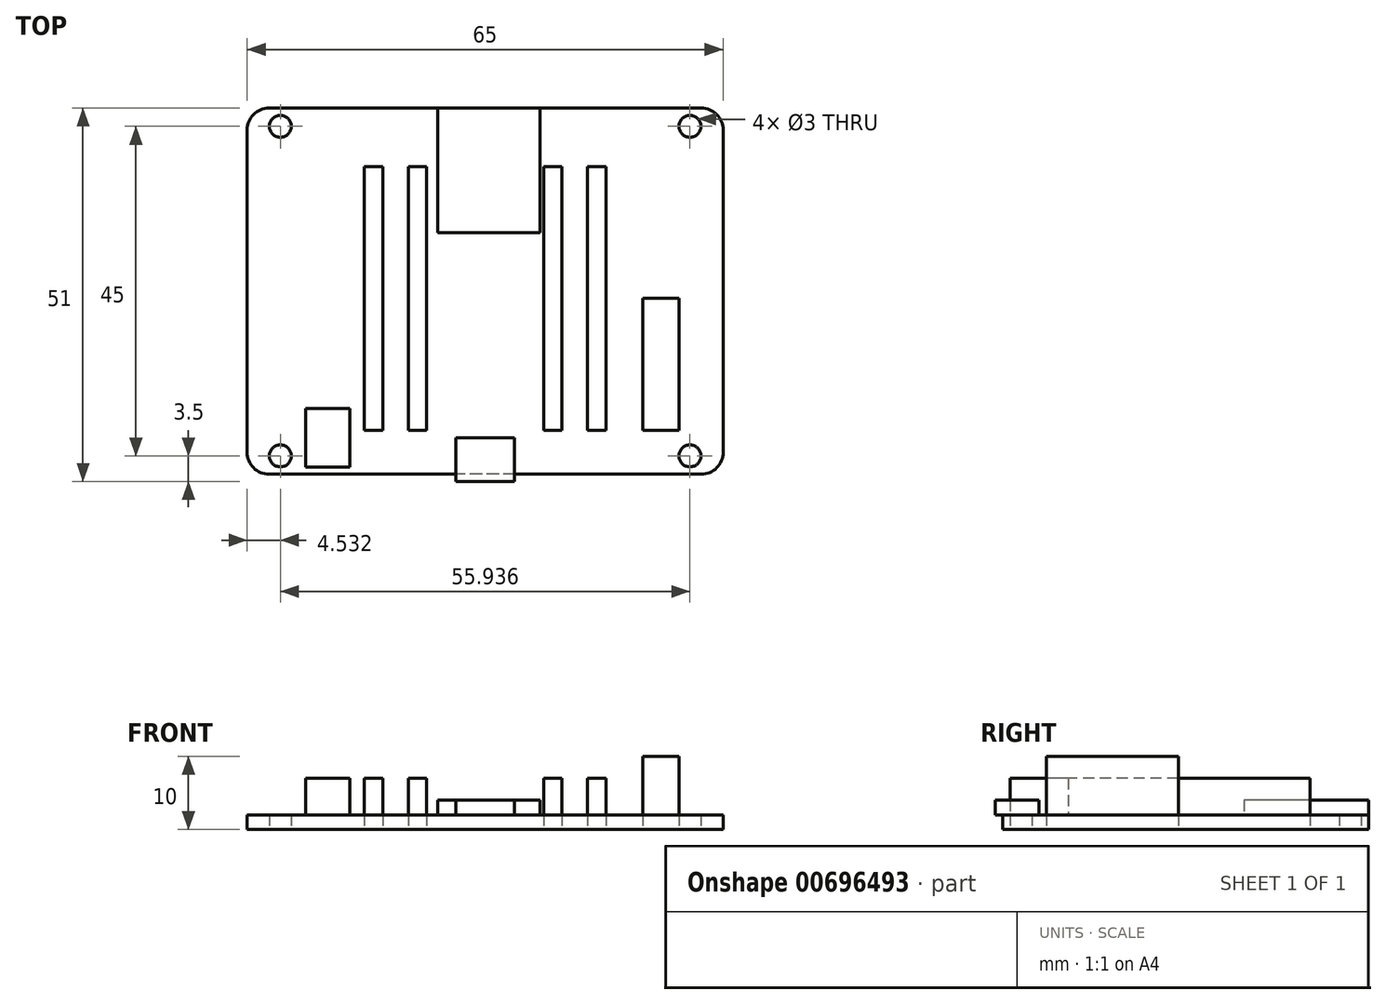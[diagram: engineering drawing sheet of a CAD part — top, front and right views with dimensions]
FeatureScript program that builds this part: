
annotation { "Feature Type Name" : "Feature", "Feature Type Description" : "" }
export const myFeature = defineFeature(function(context is Context, id is Id, definition is map)
    precondition{}
    {
        {
            var Q0;
            Q0=qCreatedBy(makeId("Top.planeOp"),FACE);
            var sketch = newSketch(context, id + "F0", { "sketchPlane" : qUnion([Q0])});
            skLineSegment(sketch, "E0.bottom", {"start": v(29.5, -25) * mm, "end": v(-29.5, -25) * mm});
            skLineSegment(sketch, "E0.top", {"start": v(29.5, 25) * mm, "end": v(-29.5, 25) * mm});
            skLineSegment(sketch, "E0.left", {"start": v(32.5, -22) * mm, "end": v(32.5, 22) * mm});
            skLineSegment(sketch, "E0.right", {"start": v(-32.5, -22) * mm, "end": v(-32.5, 22) * mm});
            skPoint(sketch, "E0.middle", {"position": v(0, 0) * mm});
            skPoint(sketch, "E1.visualSharp", {"position": v(-32.5, 25) * mm});
            skArc(sketch, "E1.filletArc", {"start": v(-29.5, 25) * mm, "mid": v(-31.62, 24.12) * mm, "end": v(-32.5, 22) * mm});
            skPoint(sketch, "E2.visualSharp", {"position": v(32.5, 25) * mm});
            skArc(sketch, "E2.filletArc", {"start": v(32.5, 22) * mm, "mid": v(31.62, 24.12) * mm, "end": v(29.5, 25) * mm});
            skPoint(sketch, "E3.visualSharp", {"position": v(32.5, -25) * mm});
            skArc(sketch, "E3.filletArc", {"start": v(29.5, -25) * mm, "mid": v(31.62, -24.12) * mm, "end": v(32.5, -22) * mm});
            skPoint(sketch, "E4.visualSharp", {"position": v(-32.5, -25) * mm});
            skArc(sketch, "E4.filletArc", {"start": v(-32.5, -22) * mm, "mid": v(-31.62, -24.12) * mm, "end": v(-29.5, -25) * mm});
            skCircle(sketch, "E5", {"center": v(-27.97, 22.5) * mm, "radius": 1.5 * mm});
            skLineSegment(sketch, "E6", {"start": v(-27.97, 24) * mm, "end": v(-27.97, 25) * mm, "construction": true});
            skLineSegment(sketch, "E7", {"start": v(-29.47, 22.45) * mm, "end": v(-32.47, 22.45) * mm, "construction": true});
            skLineSegment(sketch, "E8.MirrorCS", {"start": v(27.97, 24) * mm, "end": v(27.97, 25) * mm, "construction": true});
            skLineSegment(sketch, "E9.MirrorCS", {"start": v(29.47, 22.45) * mm, "end": v(32.47, 22.45) * mm, "construction": true});
            skCircle(sketch, "E10.MirrorC", {"center": v(27.97, 22.5) * mm, "radius": 1.5 * mm});
            skLineSegment(sketch, "E11.MirrorCS", {"start": v(-29.47, -22.45) * mm, "end": v(-32.47, -22.45) * mm, "construction": true});
            skLineSegment(sketch, "E12.MirrorCS", {"start": v(-27.97, -24) * mm, "end": v(-27.97, -25) * mm, "construction": true});
            skCircle(sketch, "E13.MirrorC", {"center": v(-27.97, -22.5) * mm, "radius": 1.5 * mm});
            skArc(sketch, "E14.MirrorCS", {"start": v(-29.5, -25) * mm, "mid": v(-31.62, -24.12) * mm, "end": v(-32.5, -22) * mm});
            skCircle(sketch, "E15.MirrorC", {"center": v(27.97, -22.5) * mm, "radius": 1.5 * mm});
            skLineSegment(sketch, "E16.bottom", {"start": v(21.5, -19) * mm, "end": v(26.5, -19) * mm});
            skLineSegment(sketch, "E16.top", {"start": v(21.5, -1) * mm, "end": v(26.5, -1) * mm});
            skLineSegment(sketch, "E16.left", {"start": v(21.5, -19) * mm, "end": v(21.5, -1) * mm});
            skLineSegment(sketch, "E16.right", {"start": v(26.5, -19) * mm, "end": v(26.5, -1) * mm});
            skLineSegment(sketch, "E17", {"start": v(24, -19) * mm, "end": v(24, -25) * mm, "construction": true});
            skLineSegment(sketch, "E18", {"start": v(26.5, -13.01) * mm, "end": v(32.5, -13.01) * mm, "construction": true});
            skLineSegment(sketch, "E19.bottom", {"start": v(-6.5, 26) * mm, "end": v(7.5, 26) * mm});
            skLineSegment(sketch, "E19.top", {"start": v(-6.5, 8) * mm, "end": v(7.5, 8) * mm});
            skLineSegment(sketch, "E19.left", {"start": v(-6.5, 26) * mm, "end": v(-6.5, 8) * mm});
            skLineSegment(sketch, "E19.right", {"start": v(7.5, 26) * mm, "end": v(7.5, 8) * mm});
            skLineSegment(sketch, "E20", {"start": v(-6.62, 26) * mm, "end": v(-6.62, 25) * mm, "construction": true});
            skLineSegment(sketch, "E21", {"start": v(7.5, 14.4) * mm, "end": v(32.5, 14.4) * mm, "construction": true});
            skLineSegment(sketch, "E22.bottom", {"start": v(14, 17) * mm, "end": v(16.5, 17) * mm});
            skLineSegment(sketch, "E22.top", {"start": v(14, -19) * mm, "end": v(16.5, -19) * mm});
            skLineSegment(sketch, "E22.left", {"start": v(14, 17) * mm, "end": v(14, -19) * mm});
            skLineSegment(sketch, "E22.right", {"start": v(16.5, 17) * mm, "end": v(16.5, -19) * mm});
            skLineSegment(sketch, "E23", {"start": v(15.25, -19) * mm, "end": v(15.25, -25) * mm, "construction": true});
            skLineSegment(sketch, "E24", {"start": v(16.5, 5.64) * mm, "end": v(32.5, 5.64) * mm, "construction": true});
            skLineSegment(sketch, "E25.1.0.0", {"start": v(8, 17) * mm, "end": v(8, -19) * mm});
            skLineSegment(sketch, "E25.1.0.1", {"start": v(8, 17) * mm, "end": v(10.5, 17) * mm});
            skLineSegment(sketch, "E25.1.0.2", {"start": v(10.5, 17) * mm, "end": v(10.5, -19) * mm});
            skLineSegment(sketch, "E25.1.0.3", {"start": v(8, -19) * mm, "end": v(10.5, -19) * mm});
            skLineSegment(sketch, "E25.direction1", {"start": v(8, -19) * mm, "end": v(14, -19) * mm, "construction": true});
            skLineSegment(sketch, "E26.MirrorCS", {"start": v(-14, -19) * mm, "end": v(-16.5, -19) * mm});
            skLineSegment(sketch, "E27.MirrorCS", {"start": v(-15.25, -19) * mm, "end": v(-15.25, -25) * mm, "construction": true});
            skLineSegment(sketch, "E28.MirrorCS", {"start": v(-8, -19) * mm, "end": v(-10.5, -19) * mm});
            skLineSegment(sketch, "E29.MirrorCS", {"start": v(-16.5, 17) * mm, "end": v(-16.5, -19) * mm});
            skLineSegment(sketch, "E30.MirrorCS", {"start": v(-14, 17) * mm, "end": v(-14, -19) * mm});
            skLineSegment(sketch, "E31.MirrorCS", {"start": v(-8, -19) * mm, "end": v(-14, -19) * mm, "construction": true});
            skLineSegment(sketch, "E32.MirrorCS", {"start": v(-16.5, 5.64) * mm, "end": v(-32.5, 5.64) * mm, "construction": true});
            skLineSegment(sketch, "E33.MirrorCS", {"start": v(-8, 17) * mm, "end": v(-8, -19) * mm});
            skLineSegment(sketch, "E34.MirrorCS", {"start": v(-7.5, 14.4) * mm, "end": v(-32.5, 14.4) * mm, "construction": true});
            skLineSegment(sketch, "E35.MirrorCS", {"start": v(-10.5, 17) * mm, "end": v(-10.5, -19) * mm});
            skLineSegment(sketch, "E36.MirrorCS", {"start": v(-14, 17) * mm, "end": v(-16.5, 17) * mm});
            skLineSegment(sketch, "E37.MirrorCS", {"start": v(-8, 17) * mm, "end": v(-10.5, 17) * mm});
            skLineSegment(sketch, "E38.bottom", {"start": v(-4, -20) * mm, "end": v(4, -20) * mm});
            skLineSegment(sketch, "E38.top", {"start": v(-4, -26) * mm, "end": v(4, -26) * mm});
            skLineSegment(sketch, "E38.left", {"start": v(-4, -20) * mm, "end": v(-4, -26) * mm});
            skLineSegment(sketch, "E38.right", {"start": v(4, -20) * mm, "end": v(4, -26) * mm});
            skLineSegment(sketch, "E39", {"start": v(-1.87, -25) * mm, "end": v(-1.87, -26) * mm, "construction": true});
            skLineSegment(sketch, "E40", {"start": v(-4, -20.58) * mm, "end": v(-32.5, -20.58) * mm, "construction": true});
            skLineSegment(sketch, "E41.bottom", {"start": v(-24.5, -16) * mm, "end": v(-18.5, -16) * mm});
            skLineSegment(sketch, "E41.top", {"start": v(-24.5, -24) * mm, "end": v(-18.5, -24) * mm});
            skLineSegment(sketch, "E41.left", {"start": v(-24.5, -16) * mm, "end": v(-24.5, -24) * mm});
            skLineSegment(sketch, "E41.right", {"start": v(-18.5, -16) * mm, "end": v(-18.5, -24) * mm});
            skLineSegment(sketch, "E42", {"start": v(-20.96, -25) * mm, "end": v(-20.96, -24) * mm, "construction": true});
            skLineSegment(sketch, "E43", {"start": v(-32.5, -17.68) * mm, "end": v(-24.5, -17.68) * mm, "construction": true});
            skSolve(sketch);
        }
        {
            var Q0;
            Q0=makeQuery(id+"F0.imprint","IMPRINT",FACE,{"disambiguationData":[TD([[makeQuery(id+"F0.imprint","IMPRINT",EDGE,{"derivedFrom":sQuery(id+"F0.wireOp",EDGE,"E0.left")}),1.0]])]});
            var Q1;
            Q1=makeQuery(id+"F0.imprint","IMPRINT",FACE,{"disambiguationData":[TD([[makeQuery(id+"F0.imprint","IMPRINT",EDGE,{"derivedFrom":sQuery(id+"F0.wireOp",EDGE,"E41.bottom")}),-1.0]])]});
            var Q2;
            Q2=makeQuery(id+"F0.imprint","IMPRINT",FACE,{"disambiguationData":[TD([[makeQuery(id+"F0.imprint","IMPRINT",EDGE,{"derivedFrom":sQuery(id+"F0.wireOp",EDGE,"E26.MirrorCS")}),-1.0]])]});
            var Q3;
            Q3=makeQuery(id+"F0.imprint","IMPRINT",FACE,{"disambiguationData":[TD([[makeQuery(id+"F0.imprint","IMPRINT",EDGE,{"derivedFrom":sQuery(id+"F0.wireOp",EDGE,"E28.MirrorCS")}),-1.0]])]});
            var Q4;
            {var subQ5=sQuery(id+"F0.wireOp",EDGE,"E38.bottom");Q4=makeQuery(id+"F0.imprint","IMPRINT",FACE,{"disambiguationData":[TD([[makeQuery(id+"F0.imprint","IMPRINT",EDGE,{"derivedFrom":subQ5}),-1.0]])]});}
            var Q5;
            Q5=makeQuery(id+"F0.imprint","IMPRINT",FACE,{"disambiguationData":[TD([[makeQuery(id+"F0.imprint","IMPRINT",EDGE,{"derivedFrom":sQuery(id+"F0.wireOp",EDGE,"E25.1.0.0")}),1.0]])]});
            var Q6;
            Q6=makeQuery(id+"F0.imprint","IMPRINT",FACE,{"disambiguationData":[TD([[makeQuery(id+"F0.imprint","IMPRINT",EDGE,{"derivedFrom":sQuery(id+"F0.wireOp",EDGE,"E22.bottom")}),-1.0]])]});
            var Q7;
            Q7=makeQuery(id+"F0.imprint","IMPRINT",FACE,{"disambiguationData":[TD([[makeQuery(id+"F0.imprint","IMPRINT",EDGE,{"derivedFrom":sQuery(id+"F0.wireOp",EDGE,"E16.bottom")}),1.0]])]});
            var Q8;
            {var subQ5=sQuery(id+"F0.wireOp",EDGE,"E19.top");Q8=makeQuery(id+"F0.imprint","IMPRINT",FACE,{"disambiguationData":[TD([[makeQuery(id+"F0.imprint","IMPRINT",EDGE,{"derivedFrom":subQ5}),1.0]])]});}
            extrude(context, id + "F1", {"entities" : qUnion([Q0, Q1, Q2, Q3, Q4, Q5, Q6, Q7, Q8]), "depth" : 2 * mm, "offsetDistance" : 25 * mm});
        }
        {
            var Q0;
            Q0=makeQuery(id+"F0.imprint","IMPRINT",FACE,{"disambiguationData":[TD([[makeQuery(id+"F0.imprint","IMPRINT",EDGE,{"derivedFrom":sQuery(id+"F0.wireOp",EDGE,"E25.1.0.0")}),1.0]])]});
            var Q1;
            Q1=makeQuery(id+"F0.imprint","IMPRINT",FACE,{"disambiguationData":[TD([[makeQuery(id+"F0.imprint","IMPRINT",EDGE,{"derivedFrom":sQuery(id+"F0.wireOp",EDGE,"E22.bottom")}),-1.0]])]});
            var Q2;
            Q2=makeQuery(id+"F0.imprint","IMPRINT",FACE,{"disambiguationData":[TD([[makeQuery(id+"F0.imprint","IMPRINT",EDGE,{"derivedFrom":sQuery(id+"F0.wireOp",EDGE,"E28.MirrorCS")}),-1.0]])]});
            var Q3;
            Q3=makeQuery(id+"F0.imprint","IMPRINT",FACE,{"disambiguationData":[TD([[makeQuery(id+"F0.imprint","IMPRINT",EDGE,{"derivedFrom":sQuery(id+"F0.wireOp",EDGE,"E26.MirrorCS")}),-1.0]])]});
            extrude(context, id + "F2", {"entities" : qUnion([Q0, Q1, Q2, Q3]), "depth" : 7 * mm, "offsetDistance" : 25 * mm});
        }
        {
            var Q0;
            {var subQ5=sQuery(id+"F0.wireOp",EDGE,"E19.top");Q0=makeQuery(id+"F0.imprint","IMPRINT",FACE,{"disambiguationData":[TD([[makeQuery(id+"F0.imprint","IMPRINT",EDGE,{"derivedFrom":subQ5}),1.0]])]});}
            extrude(context, id + "F3", {"entities" : qUnion([Q0]), "depth" : 4 * mm, "offsetDistance" : 25 * mm, "hasSecondDirection" : true, "secondDirectionOppositeDirection" : true, "secondDirectionDepth" : -2 * mm});
        }
        {
            var Q0;
            Q0=makeQuery(id+"F0.imprint","IMPRINT",FACE,{"disambiguationData":[TD([[makeQuery(id+"F0.imprint","IMPRINT",EDGE,{"derivedFrom":sQuery(id+"F0.wireOp",EDGE,"E16.bottom")}),1.0]])]});
            extrude(context, id + "F4", {"entities" : qUnion([Q0]), "depth" : 10 * mm, "offsetDistance" : 25 * mm});
        }
        {
            var Q0;
            {var subQ5=sQuery(id+"F0.wireOp",EDGE,"E38.bottom");Q0=makeQuery(id+"F0.imprint","IMPRINT",FACE,{"disambiguationData":[TD([[makeQuery(id+"F0.imprint","IMPRINT",EDGE,{"derivedFrom":subQ5}),-1.0]])]});}
            var Q1;
            {var subQ5=sQuery(id+"F0.wireOp",EDGE,"E38.top");Q1=makeQuery(id+"F0.imprint","IMPRINT",FACE,{"disambiguationData":[TD([[makeQuery(id+"F0.imprint","IMPRINT",EDGE,{"derivedFrom":subQ5}),1.0]])]});}
            extrude(context, id + "F5", {"entities" : qUnion([Q0, Q1]), "depth" : 4 * mm, "offsetDistance" : 25 * mm, "hasSecondDirection" : true, "secondDirectionOppositeDirection" : true, "secondDirectionDepth" : -2 * mm});
        }
        {
            var Q0;
            Q0=makeQuery(id+"F0.imprint","IMPRINT",FACE,{"disambiguationData":[TD([[makeQuery(id+"F0.imprint","IMPRINT",EDGE,{"derivedFrom":sQuery(id+"F0.wireOp",EDGE,"E41.bottom")}),-1.0]])]});
            extrude(context, id + "F6", {"entities" : qUnion([Q0]), "depth" : 7 * mm, "offsetDistance" : 25 * mm, "hasSecondDirection" : true, "secondDirectionOppositeDirection" : true, "secondDirectionDepth" : -2 * mm});
        }
    });
